# Revit family: 05-1804-14-00
name_source: partatom
category: Luminarias
revit_build: Autodesk Revit 2017 (Build: 20160225_1515(x64)
units: mm (PartAtom-declared; Revit-internal decimal feet)

## family parameters
Anfitrión = Cara
Compartido = Sí
Corte con vacíos al cargar = No
Cota de conector redondo = Diámetro de uso
Número OmniClass = 23.80.70.00
Origen de luz = No
Punto de cálculo de habitación = No
Tipo de pieza = Normal
Título OmniClass = Lighting

## types (1)
- 05-1804-14-00
    Acabado = Blanco
    CRI = 80
    Carga aparente = 0 VA
    Catálogo = Technical
    CodigoGubimclass = 50.60.50.20
    CodigoOmniclass = 21-04 50 40
    CodigoUniclass2015 = EF_70_80
    CodigoUniformat2010 = D5040
    DescripcionGubimclass = Iluminación interior
    DescripcionOmniclass = Lighting
    DescripcionUniclass2015 = Lighting
    DescripcionUniformat2010 = Lighting
    EAN13 = 8435381400750
    Eficiencia energética = LED A++
    Elevación por defecto = 1000 mm  [stored 3.28084 ft]
    Etiqueta V/f = max. 350mA
    Fabricante = LEDS C4
    Familia = Secret A
    FechaVersion = Julio 2020
    Ficha = http://files.leds-c4.com
    Fotometría = http://files.leds-c4.com
    Fuente de luz = 1xLED 1 87.00 lm
    IMC = http://files.leds-c4.com
    IP = IP20
    IfcExportAs = IfcLightFixture
IfcLightFixture
    IfcExportType = NOTDEFINED
    Imagen web = http://files.leds-c4.com
    LDT = http://files.leds-c4.com
    Lumenes reales (lm) = 43
    Material = Yeso
    Peso neto (KG) = 0.52
    Pluma comercial = http://files.leds-c4.com
    Producto descatalogado = Catalogado ES
    Referencia = 05-1804-14-00
    Temperatura color led (K) = Blanco cálido - 3000K
    Tender text (Castellano) = LEDS C4
Secret A
05-1804-14-00

Luminaria de señalización de uso interior para iluminar frontalmente y hacia abajo. 

Uso de lentes para un óptimo control lumínico y minimización del halo residual. Material estructura: Yeso. Acabado estructura: Blanco. Garantía: 5 Años.

Peso neto del producto (Kg): 0.520
Anchura o diámetro del producto (mm): 80
Altura del producto (mm): 165
Ø del agujero para empotrar (mm): 170x85
Grosor de techo admitido: 9-15

Clase 3. IP: IP20. LED. Nº de portalámparas o Leds: 1. Marca del LED: CREE. Potencia máxima de la fuente de luz: 1W. Temperatura de color: Blanco cálido - 3000K. Índice de reproducción cromática: 80. Steps Mac Adam: 3. Diámetro máximo de la bombilla que admite la luminaria: 50.000h L80B20. UGR: 5.5. Riesgo fotobiológico: RG2. Flujo real (lm): 43. Flujo nominal (lm): 87. Lm/W reales: 43. Voltaje: 3. Equipo incluido: No, pero lo necesita. Potencia total: 1.
    Tender text (English) = LEDS C4
Secret A
05-1804-14-00

Signal lighting/light for indoor use. 

For frontal lighting and downlighting. Lenses allow optimum control of illumination with minimal residual halo. Structure material: Plaster. Structure finish: White. Warranty: 5 Years.

Product net weight (Kg): 0.520
Product width or diameter (mm): 80
Product height (mm): 165
Ø of the hole for recessing (mm): 170x85
Permitted ceiling thickness: 9-15

Class 3. IP: IP20. LED. No. of lampholders or LEDs: 1. LED brand: CREE. Maximum power of light source: 1W. Colour temperature: LED warm-white 3000K. Colour rendering index: 80. MacAdam Steps: 3. Maximum diameter of luminaire bulb: 50.000h L80B20. UGR: 5.5. Photobiological risk: RG2. Real flux (lm): 43. Nominal flux (lm): 87. Lm/Real W: 43. Voltage: 3. Gear included: No, but it is needed. Total power: 1.
    Tipo = Señalizacion
    Vatios (W) = 1
    Versión = v1

note: [stored X ft] marks values corroborated as IEEE doubles in the binary element streams (Revit-internal decimal feet)
